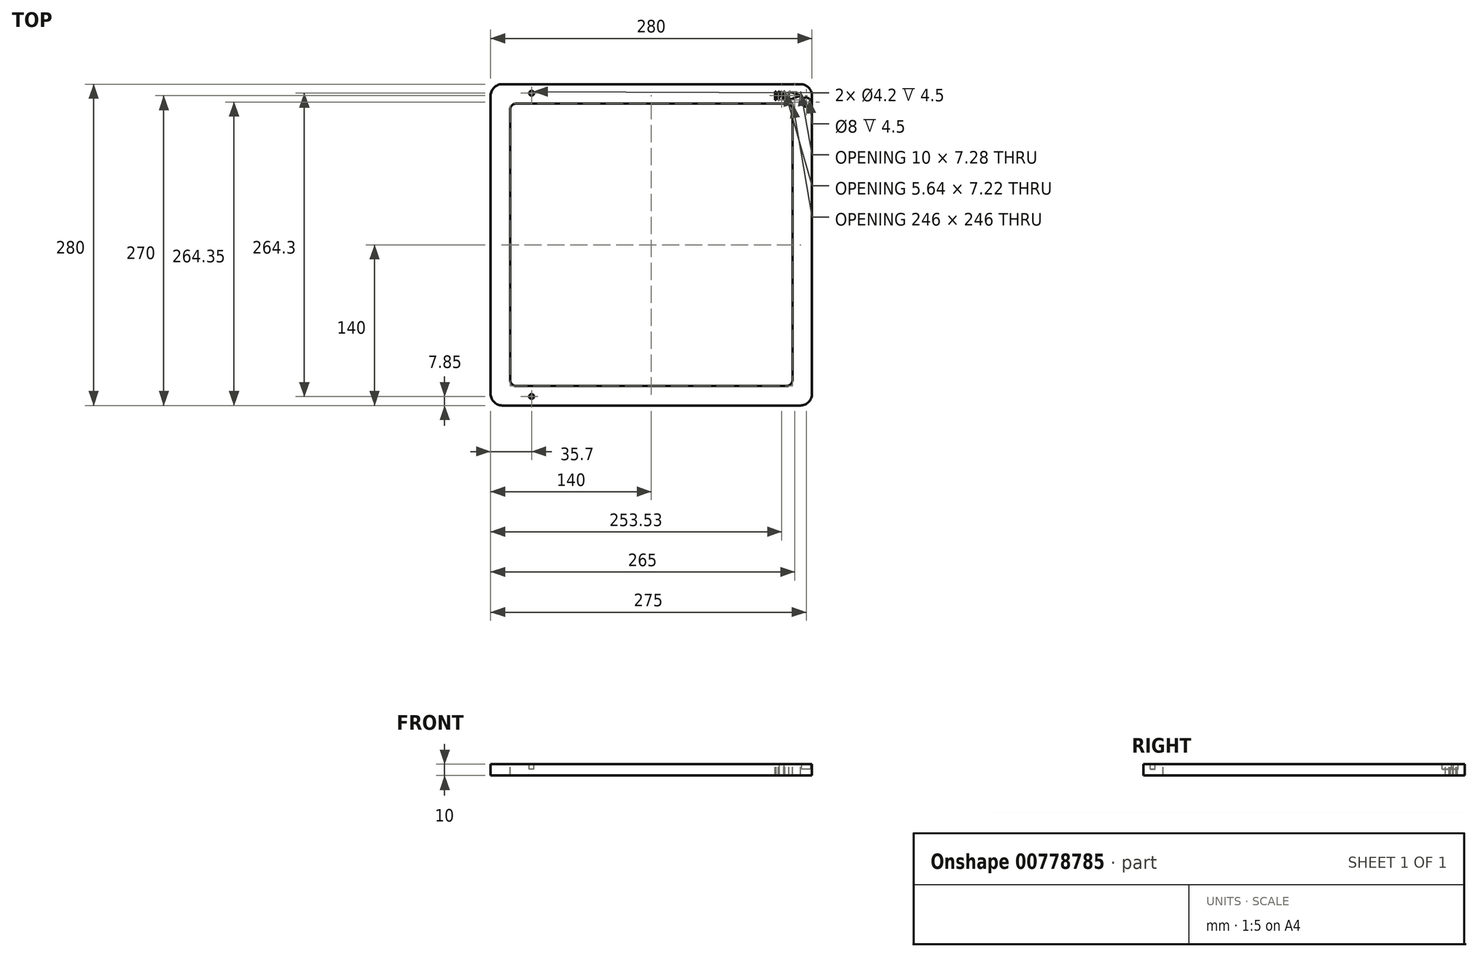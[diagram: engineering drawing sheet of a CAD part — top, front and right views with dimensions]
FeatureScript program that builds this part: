
annotation { "Feature Type Name" : "Feature", "Feature Type Description" : "" }
export const myFeature = defineFeature(function(context is Context, id is Id, definition is map)
    precondition{}
    {
        {
            var Q0;
            Q0=qCreatedBy(makeId("Top.planeOp"),FACE);
            var sketch = newSketch(context, id + "F0", { "sketchPlane" : qUnion([Q0])});
            skLineSegment(sketch, "E0.bottom", {"start": v(130, 140) * mm, "end": v(-130, 140) * mm});
            skLineSegment(sketch, "E0.top", {"start": v(130, -140) * mm, "end": v(-130, -140) * mm});
            skLineSegment(sketch, "E0.left", {"start": v(140, 130) * mm, "end": v(140, -130) * mm});
            skLineSegment(sketch, "E0.right", {"start": v(-140, 130) * mm, "end": v(-140, -130) * mm});
            skPoint(sketch, "E0.middle", {"position": v(0, 0) * mm});
            skPoint(sketch, "E1.visualSharp", {"position": v(-140, 140) * mm});
            skArc(sketch, "E1.filletArc", {"start": v(-130, 140) * mm, "mid": v(-137.07, 137.07) * mm, "end": v(-140, 130) * mm});
            skPoint(sketch, "E2.visualSharp", {"position": v(140, 140) * mm});
            skArc(sketch, "E2.filletArc", {"start": v(140, 130) * mm, "mid": v(137.07, 137.07) * mm, "end": v(130, 140) * mm});
            skPoint(sketch, "E3.visualSharp", {"position": v(140, -140) * mm});
            skArc(sketch, "E3.filletArc", {"start": v(130, -140) * mm, "mid": v(137.07, -137.07) * mm, "end": v(140, -130) * mm});
            skPoint(sketch, "E4.visualSharp", {"position": v(-140, -140) * mm});
            skArc(sketch, "E4.filletArc", {"start": v(-140, -130) * mm, "mid": v(-137.07, -137.07) * mm, "end": v(-130, -140) * mm});
            skSolve(sketch);
        }
        {
            var Q0;
            Q0=qSketchRegion(id+"F0",true);
            extrude(context, id + "F1", {"entities" : qUnion([Q0]), "depth" : 10 * mm, "offsetDistance" : 25 * mm});
        }
        {
            var Q0;
            Q0=makeQuery(id+"F1.opExtrude","CAP_FACE",FACE,{"disambiguationData":[OSD([sQuery(id+"F0.wireOp",EDGE,"E0.bottom"),sQuery(id+"F0.wireOp",EDGE,"E0.top"),sQuery(id+"F0.wireOp",EDGE,"E0.left"),sQuery(id+"F0.wireOp",EDGE,"E0.right"),sQuery(id+"F0.wireOp",EDGE,"E1.filletArc"),sQuery(id+"F0.wireOp",EDGE,"E2.filletArc"),sQuery(id+"F0.wireOp",EDGE,"E3.filletArc"),sQuery(id+"F0.wireOp",EDGE,"E4.filletArc")])],"isStart":false});
            var sketch = newSketch(context, id + "F2", { "sketchPlane" : qUnion([Q0])});
            skLineSegment(sketch, "E5", {"start": v(-104.3, -132.15) * mm, "end": v(-104.3, 0) * mm, "construction": true});
            skLineSegment(sketch, "E6", {"start": v(-104.3, 0) * mm, "end": v(-104.3, 132.15) * mm, "construction": true});
            skCircle(sketch, "E7", {"center": v(-104.3, 132.15) * mm, "radius": 2.1 * mm});
            skCircle(sketch, "E8", {"center": v(135, 124.35) * mm, "radius": 4 * mm});
            skCircle(sketch, "E9", {"center": v(-104.3, -132.15) * mm, "radius": 2.1 * mm});
            skSolve(sketch);
        }
        {
            var Q0;
            Q0=qSketchRegion(id+"F2",true);
            extrude(context, id + "F3", {"entities" : qUnion([Q0]), "operationType" : NewBodyOperationType.REMOVE, "oppositeDirection" : true, "depth" : 4.5 * mm, "offsetDistance" : 25 * mm});
        }
        {
            var Q0;
            Q0=makeQuery(id+"F1.opExtrude","CAP_FACE",FACE,{"disambiguationData":[OSD([sQuery(id+"F0.wireOp",EDGE,"E0.bottom"),sQuery(id+"F0.wireOp",EDGE,"E0.top"),sQuery(id+"F0.wireOp",EDGE,"E0.left"),sQuery(id+"F0.wireOp",EDGE,"E0.right"),sQuery(id+"F0.wireOp",EDGE,"E1.filletArc"),sQuery(id+"F0.wireOp",EDGE,"E2.filletArc"),sQuery(id+"F0.wireOp",EDGE,"E3.filletArc"),sQuery(id+"F0.wireOp",EDGE,"E4.filletArc")])],"isStart":false});
            var sketch = newSketch(context, id + "F4", { "sketchPlane" : qUnion([Q0])});
            skLineSegment(sketch, "E10", {"start": v(130, 130) * mm, "end": v(120, 133.64) * mm});
            skLineSegment(sketch, "E11", {"start": v(120, 133.64) * mm, "end": v(120, 126.36) * mm});
            skLineSegment(sketch, "E12", {"start": v(120, 126.36) * mm, "end": v(130, 130) * mm});
            skLineSegment(sketch, "E13", {"start": v(130, 130) * mm, "end": v(120, 130) * mm, "construction": true});
            skText(sketch, "E14", { "text": "IN", "fontName": "OpenSans-Regular.ttf"});
            skLineSegment(sketch, "E15.bottom", {"start": v(-118, 123) * mm, "end": v(118, 123) * mm});
            skLineSegment(sketch, "E15.top", {"start": v(-118, -123) * mm, "end": v(118, -123) * mm});
            skLineSegment(sketch, "E15.left", {"start": v(-123, 118) * mm, "end": v(-123, -118) * mm});
            skLineSegment(sketch, "E15.right", {"start": v(123, 118) * mm, "end": v(123, -118) * mm});
            skPoint(sketch, "E15.middle", {"position": v(0, 0) * mm});
            skPoint(sketch, "E16.visualSharp", {"position": v(-123, 123) * mm});
            skArc(sketch, "E16.filletArc", {"start": v(-118, 123) * mm, "mid": v(-121.54, 121.54) * mm, "end": v(-123, 118) * mm});
            skPoint(sketch, "E17.visualSharp", {"position": v(123, 123) * mm});
            skArc(sketch, "E17.filletArc", {"start": v(123, 118) * mm, "mid": v(121.54, 121.54) * mm, "end": v(118, 123) * mm});
            skPoint(sketch, "E18.visualSharp", {"position": v(123, -123) * mm});
            skArc(sketch, "E18.filletArc", {"start": v(118, -123) * mm, "mid": v(121.54, -121.54) * mm, "end": v(123, -118) * mm});
            skPoint(sketch, "E19.visualSharp", {"position": v(-123, -123) * mm});
            skArc(sketch, "E19.filletArc", {"start": v(-123, -118) * mm, "mid": v(-121.54, -121.54) * mm, "end": v(-118, -123) * mm});
            const initialGuessF4  = {"E14": [0.1069, 0.12636, 1, 0, 0.00728]};
            skSetInitialGuess(sketch, initialGuessF4);
            skSolve(sketch);
        }
        {
            var Q0;
            Q0=qSketchRegion(id+"F4",true);
            var Q1;
            Q1=makeQuery(id+"F1.opExtrude","CAP_FACE",FACE,{"disambiguationData":[OSD([sQuery(id+"F0.wireOp",EDGE,"E0.bottom"),sQuery(id+"F0.wireOp",EDGE,"E0.top"),sQuery(id+"F0.wireOp",EDGE,"E0.left"),sQuery(id+"F0.wireOp",EDGE,"E0.right"),sQuery(id+"F0.wireOp",EDGE,"E1.filletArc"),sQuery(id+"F0.wireOp",EDGE,"E2.filletArc"),sQuery(id+"F0.wireOp",EDGE,"E3.filletArc"),sQuery(id+"F0.wireOp",EDGE,"E4.filletArc")])],"isStart":true});
            extrude(context, id + "F5", {"entities" : qUnion([Q0, Q1]), "operationType" : NewBodyOperationType.REMOVE, "endBound" : BoundingType.THROUGH_ALL, "oppositeDirection" : true, "depth" : .1 * mm, "offsetDistance" : 25 * mm});
        }
    });
